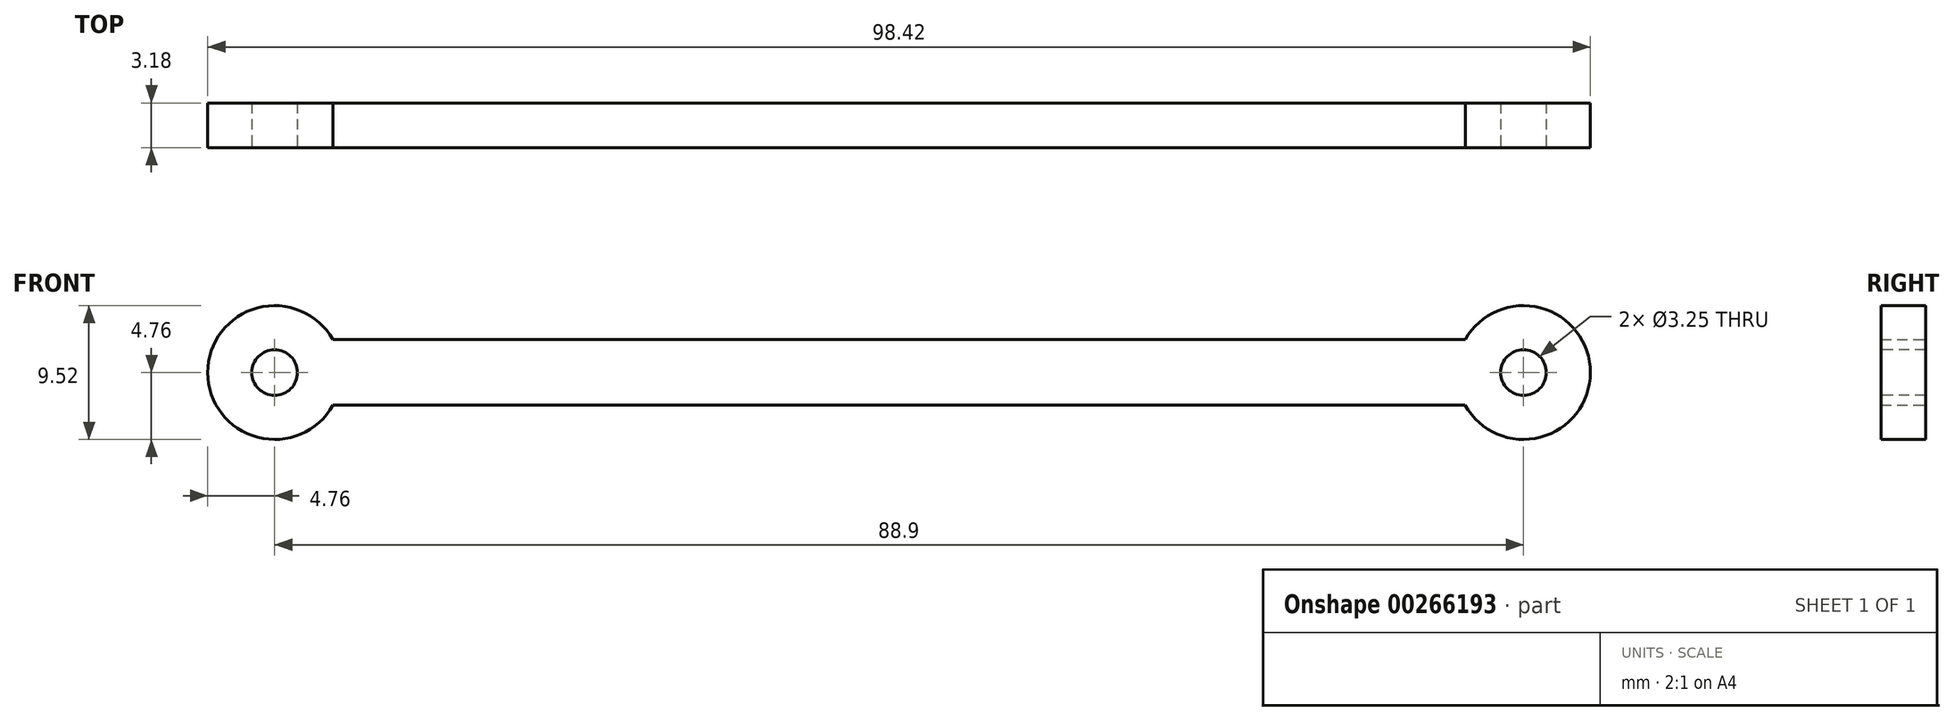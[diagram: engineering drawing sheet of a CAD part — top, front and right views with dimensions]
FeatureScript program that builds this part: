
annotation { "Feature Type Name" : "Feature", "Feature Type Description" : "" }
export const myFeature = defineFeature(function(context is Context, id is Id, definition is map)
    precondition{}
    {
        {
            var Q0;
            Q0=qCreatedBy(makeId("Front.planeOp"),FACE);
            var sketch = newSketch(context, id + "F0", { "sketchPlane" : qUnion([Q0])});
            skCircle(sketch, "E0", {"center": v(0, 0) * mm, "radius": 4.76 * mm});
            skCircle(sketch, "E1", {"center": v(88.9, 0) * mm, "radius": 4.76 * mm});
            skLineSegment(sketch, "E2", {"start": v(0, 2.34) * mm, "end": v(88.9, 2.34) * mm});
            skLineSegment(sketch, "E3", {"start": v(88.9, -2.33) * mm, "end": v(0, -2.33) * mm});
            skSolve(sketch);
        }
        {
            var Q0;
            {var subQ0=sQuery(id+"F0.wireOp",EDGE,"E2");var subQ1=sQuery(id+"F0.wireOp",EDGE,"E0");var subQ2=makeQuery(id+"F0.imprint","INTERSECT",VERTEX,{"derivedFrom":[subQ1,subQ0]});Q0=makeQuery(id+"F0.imprint","IMPRINT",FACE,{"disambiguationData":[TD([[makeQuery(id+"F0.imprint","IMPRINT",EDGE,{"disambiguationData":[TD([[subQ2,1.0]])],"derivedFrom":subQ1}),-1.0]])]});}
            var Q1;
            {var subQ0=sQuery(id+"F0.wireOp",EDGE,"E0");var subQ1=makeQuery(id+"F0.imprint","INTERSECT",VERTEX,{"derivedFrom":[subQ0,sQuery(id+"F0.wireOp",EDGE,"E2")]});Q1=makeQuery(id+"F0.imprint","IMPRINT",FACE,{"disambiguationData":[TD([[makeQuery(id+"F0.imprint","IMPRINT",EDGE,{"disambiguationData":[TD([[subQ1,-1.0]])],"derivedFrom":subQ0}),1.0]])]});}
            var Q2;
            {var subQ0=sQuery(id+"F0.wireOp",EDGE,"E1");var subQ1=makeQuery(id+"F0.imprint","INTERSECT",VERTEX,{"derivedFrom":[subQ0,sQuery(id+"F0.wireOp",EDGE,"E2")]});Q2=makeQuery(id+"F0.imprint","IMPRINT",FACE,{"disambiguationData":[TD([[makeQuery(id+"F0.imprint","IMPRINT",EDGE,{"disambiguationData":[TD([[subQ1,-1.0]])],"derivedFrom":subQ0}),1.0]])]});}
            extrude(context, id + "F1", {"entities" : qUnion([Q0, Q1, Q2]), "depth" : 3.17 * mm});
        }
        {
            var Q0;
            Q0=makeQuery(id+"F1.opExtrude","CAP_FACE",FACE,{"disambiguationData":[OSD([sQuery(id+"F0.wireOp",EDGE,"E0"),sQuery(id+"F0.wireOp",EDGE,"E1"),sQuery(id+"F0.wireOp",EDGE,"E2"),sQuery(id+"F0.wireOp",EDGE,"E3")])],"isStart":false});
            var sketch = newSketch(context, id + "F2", { "sketchPlane" : qUnion([Q0])});
            skCircle(sketch, "E4", {"center": v(0, 0) * mm, "radius": 1.63 * mm});
            skCircle(sketch, "E5", {"center": v(88.9, 0) * mm, "radius": 1.63 * mm});
            skSolve(sketch);
        }
        {
            var Q0;
            Q0=makeQuery(id+"F2.imprint","IMPRINT",FACE,{"disambiguationData":[TD([[makeQuery(id+"F2.imprint","IMPRINT",EDGE,{"derivedFrom":sQuery(id+"F2.wireOp",EDGE,"E4")}),1.0]])]});
            var Q1;
            Q1=makeQuery(id+"F2.imprint","IMPRINT",FACE,{"disambiguationData":[TD([[makeQuery(id+"F2.imprint","IMPRINT",EDGE,{"derivedFrom":sQuery(id+"F2.wireOp",EDGE,"E5")}),1.0]])]});
            extrude(context, id + "F3", {"entities" : qUnion([Q0, Q1]), "operationType" : NewBodyOperationType.REMOVE, "oppositeDirection" : true, "depth" : 25.4 * mm});
        }
    });
